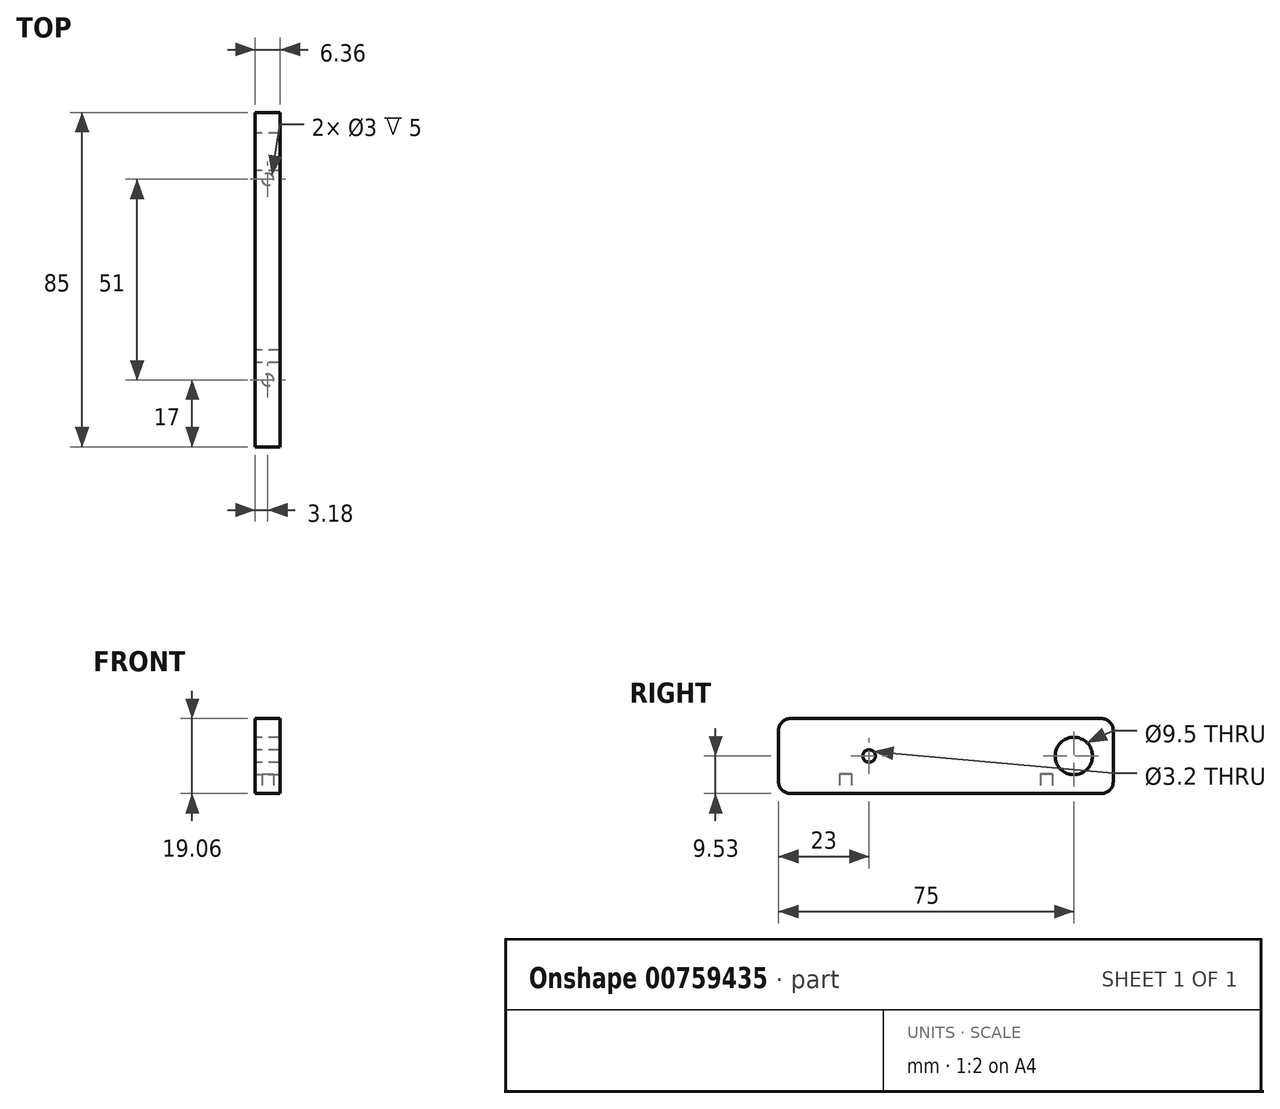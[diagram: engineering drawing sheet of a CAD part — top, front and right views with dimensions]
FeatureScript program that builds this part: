
annotation { "Feature Type Name" : "Feature", "Feature Type Description" : "" }
export const myFeature = defineFeature(function(context is Context, id is Id, definition is map)
    precondition{}
    {
        {
            var Q0;
            Q0=qCreatedBy(makeId("Right.planeOp"),FACE);
            var sketch = newSketch(context, id + "F0", { "sketchPlane" : qUnion([Q0])});
            skLineSegment(sketch, "E0.bottom", {"start": v(42.5, 9.52) * mm, "end": v(-42.5, 9.52) * mm});
            skLineSegment(sketch, "E0.top", {"start": v(42.5, -9.53) * mm, "end": v(-42.5, -9.53) * mm});
            skLineSegment(sketch, "E0.left", {"start": v(42.5, 9.52) * mm, "end": v(42.5, -9.53) * mm});
            skLineSegment(sketch, "E0.right", {"start": v(-42.5, 9.52) * mm, "end": v(-42.5, -9.53) * mm});
            skPoint(sketch, "E0.middle", {"position": v(0, 0) * mm});
            skCircle(sketch, "E1", {"center": v(32.5, 0) * mm, "radius": 4.75 * mm});
            skPoint(sketch, "E1.centerSnap0", {"position": v(42.5, 0) * mm});
            skCircle(sketch, "E2", {"center": v(-19.5, 0) * mm, "radius": 1.6 * mm});
            skSolve(sketch);
        }
        {
            var Q0;
            Q0 = qSketchRegion(id + "F0", true);
            extrude(context, id + "F1", {"entities" : qUnion([Q0]), "endBound" : BoundingType.SYMMETRIC, "depth" : 6.35 * mm, "offsetDistance" : 25 * mm});
        }
        {
            var Q0;
            Q0=makeQuery(id+"F1.opExtrude","SWEPT_FACE",FACE,{"disambiguationData":[OSD([sQuery(id+"F0.wireOp",EDGE,"E0.top")])]});
            var sketch = newSketch(context, id + "F2", { "sketchPlane" : qUnion([Q0])});
            skCircle(sketch, "E3", {"center": v(0, 25.5) * mm, "radius": 1.5 * mm});
            skPoint(sketch, "E4.center.orphan", {"position": v(0, -59.5) * mm});
            skCircle(sketch, "E5.MirrorC", {"center": v(0, -25.5) * mm, "radius": 1.5 * mm});
            skSolve(sketch);
        }
        {
            var Q0;
            Q0 = qSketchRegion(id + "F2", true);
            extrude(context, id + "F3", {"entities" : qUnion([Q0]), "operationType" : NewBodyOperationType.REMOVE, "oppositeDirection" : true, "depth" : 5 * mm, "offsetDistance" : 25 * mm});
        }
        {
            var Q0;
            Q0=makeQuery(id+"F1.opExtrude","SWEPT_EDGE",EDGE,{"disambiguationData":[OSD([sQuery(id+"F0.wireOp",EDGE,"E0.top"),sQuery(id+"F0.wireOp",EDGE,"E0.right")])]});
            var Q1;
            Q1=makeQuery(id+"F1.opExtrude","SWEPT_EDGE",EDGE,{"disambiguationData":[OSD([sQuery(id+"F0.wireOp",EDGE,"E0.bottom"),sQuery(id+"F0.wireOp",EDGE,"E0.right")])]});
            var Q2;
            Q2=makeQuery(id+"F1.opExtrude","SWEPT_EDGE",EDGE,{"disambiguationData":[OSD([sQuery(id+"F0.wireOp",EDGE,"E0.bottom"),sQuery(id+"F0.wireOp",EDGE,"E0.left")])]});
            var Q3;
            Q3=makeQuery(id+"F1.opExtrude","SWEPT_EDGE",EDGE,{"disambiguationData":[OSD([sQuery(id+"F0.wireOp",EDGE,"E0.top"),sQuery(id+"F0.wireOp",EDGE,"E0.left")])]});
            fillet(context, id + "F4", {"entities" : qUnion([Q0, Q1, Q2, Q3]), "radius" : 3 * mm, "tangentPropagation" : true, "allowEdgeOverflow" : false});
        }
    });
